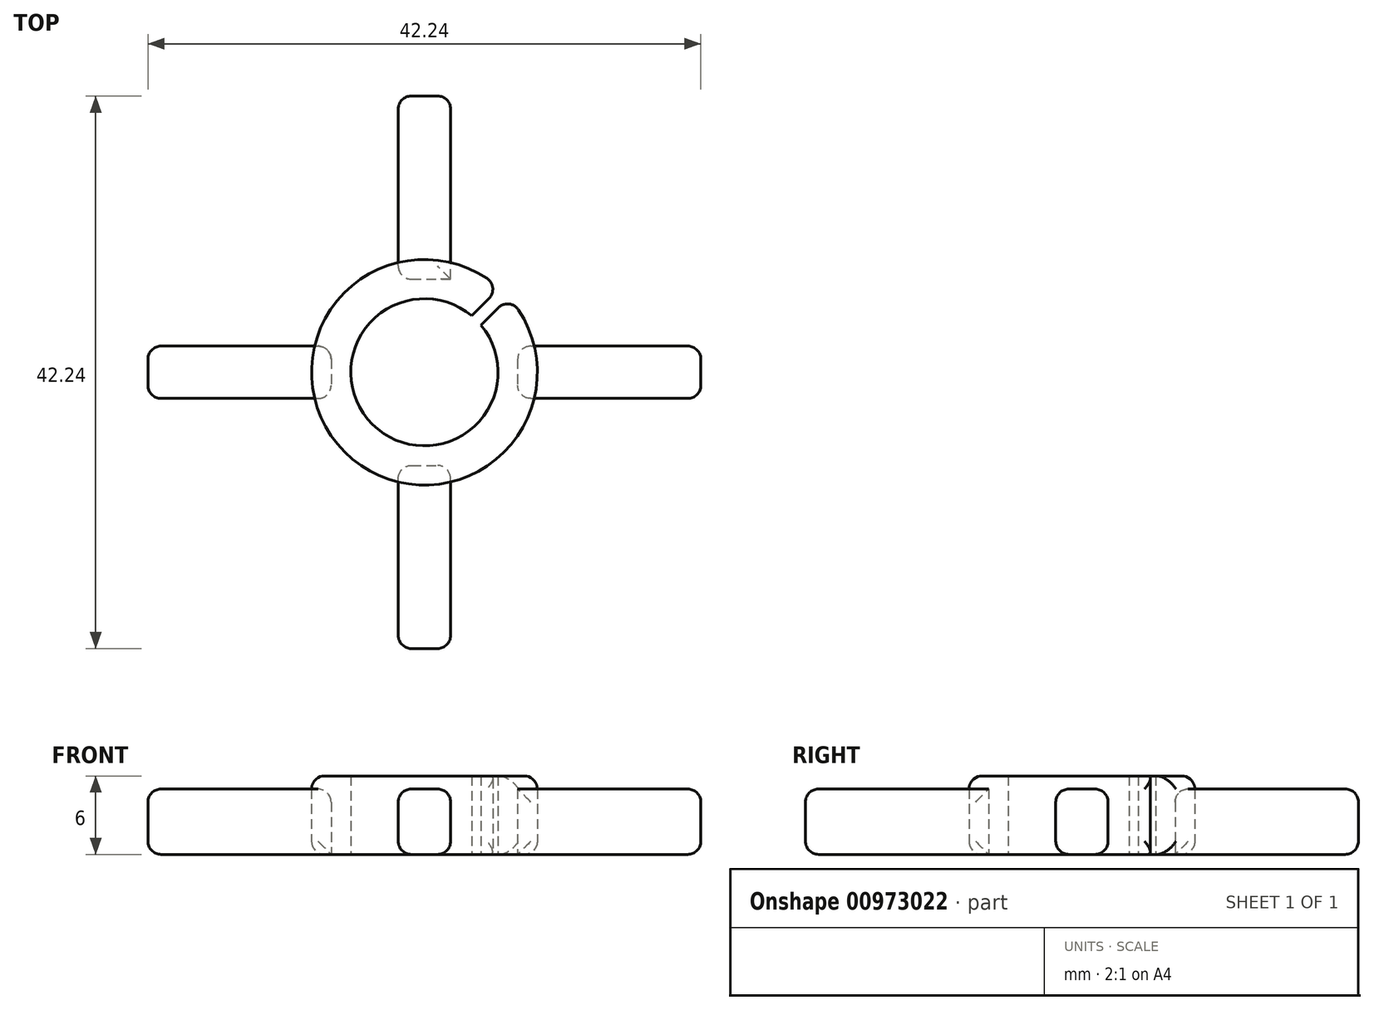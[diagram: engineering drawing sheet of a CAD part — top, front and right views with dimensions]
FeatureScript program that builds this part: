
annotation { "Feature Type Name" : "Feature", "Feature Type Description" : "" }
export const myFeature = defineFeature(function(context is Context, id is Id, definition is map)
    precondition{}
    {
        {
            var Q0;
            Q0=qCreatedBy(makeId("Top.planeOp"),FACE);
            var sketch = newSketch(context, id + "F0", { "sketchPlane" : qUnion([Q0])});
            skCircle(sketch, "E0", {"center": v(0, 0) * mm, "radius": 5.62 * mm});
            skCircle(sketch, "E1", {"center": v(0, 0) * mm, "radius": 8.62 * mm});
            skLineSegment(sketch, "E2.bottom", {"start": v(-21.12, 2) * mm, "end": v(-7.12, 2) * mm});
            skLineSegment(sketch, "E2.top", {"start": v(-21.12, -2) * mm, "end": v(-7.12, -2) * mm});
            skLineSegment(sketch, "E2.left", {"start": v(-21.12, 2) * mm, "end": v(-21.12, -2) * mm});
            skLineSegment(sketch, "E2.right", {"start": v(-7.12, 2) * mm, "end": v(-7.12, -2) * mm});
            skCircle(sketch, "E3", {"center": v(0, 0) * mm, "radius": 7.12 * mm, "construction": true});
            skPoint(sketch, "E4", {"position": v(-7.12, 0) * mm});
            skPoint(sketch, "E5", {"position": v(0, 7.12) * mm});
            skPoint(sketch, "E6", {"position": v(7.12, 0) * mm});
            skPoint(sketch, "E7", {"position": v(0, -7.12) * mm});
            skLineSegment(sketch, "E8.bottom", {"start": v(-2, 7.12) * mm, "end": v(-2, 21.12) * mm});
            skLineSegment(sketch, "E8.top", {"start": v(2, 7.12) * mm, "end": v(2, 21.12) * mm});
            skLineSegment(sketch, "E8.left", {"start": v(-2, 7.12) * mm, "end": v(2, 7.12) * mm});
            skLineSegment(sketch, "E8.right", {"start": v(-2, 21.12) * mm, "end": v(2, 21.12) * mm});
            skPoint(sketch, "E9", {"position": v(0, 21.12) * mm});
            skLineSegment(sketch, "E10.bottom", {"start": v(7.12, 2) * mm, "end": v(21.12, 2) * mm});
            skLineSegment(sketch, "E10.top", {"start": v(7.12, -2) * mm, "end": v(21.12, -2) * mm});
            skLineSegment(sketch, "E10.left", {"start": v(7.13, 2) * mm, "end": v(7.13, -2) * mm});
            skLineSegment(sketch, "E10.right", {"start": v(21.12, 2) * mm, "end": v(21.12, -2) * mm});
            skPoint(sketch, "E11", {"position": v(21.12, 0) * mm});
            skLineSegment(sketch, "E12.bottom", {"start": v(-2, -21.12) * mm, "end": v(-2, -7.12) * mm});
            skLineSegment(sketch, "E12.top", {"start": v(2, -21.12) * mm, "end": v(2, -7.12) * mm});
            skLineSegment(sketch, "E12.left", {"start": v(-2, -21.12) * mm, "end": v(2, -21.12) * mm});
            skLineSegment(sketch, "E12.right", {"start": v(-2, -7.12) * mm, "end": v(2, -7.12) * mm});
            skLineSegment(sketch, "E13.bottom", {"start": v(-0.35, 0.35) * mm, "end": v(0.35, -0.35) * mm});
            skLineSegment(sketch, "E13.top", {"start": v(13.79, 14.5) * mm, "end": v(14.5, 13.79) * mm});
            skLineSegment(sketch, "E13.left", {"start": v(-0.35, 0.35) * mm, "end": v(13.79, 14.5) * mm});
            skLineSegment(sketch, "E13.right", {"start": v(0.35, -0.35) * mm, "end": v(14.5, 13.79) * mm});
            skSolve(sketch);
        }
        {
            var Q0;
            {var subQ5=sQuery(id+"F0.wireOp",EDGE,"E2.right");Q0=makeQuery(id+"F0.imprint","IMPRINT",FACE,{"disambiguationData":[TD([[makeQuery(id+"F0.imprint","IMPRINT",EDGE,{"derivedFrom":subQ5}),-1.0]])]});}
            var Q1;
            {var subQ5=sQuery(id+"F0.wireOp",EDGE,"E8.left");Q1=makeQuery(id+"F0.imprint","IMPRINT",FACE,{"disambiguationData":[TD([[makeQuery(id+"F0.imprint","IMPRINT",EDGE,{"derivedFrom":subQ5}),1.0]])]});}
            var Q2;
            {var subQ5=sQuery(id+"F0.wireOp",EDGE,"E12.left");Q2=makeQuery(id+"F0.imprint","IMPRINT",FACE,{"disambiguationData":[TD([[makeQuery(id+"F0.imprint","IMPRINT",EDGE,{"derivedFrom":subQ5}),1.0]])]});}
            var Q3;
            {var subQ5=sQuery(id+"F0.wireOp",EDGE,"E12.right");Q3=makeQuery(id+"F0.imprint","IMPRINT",FACE,{"disambiguationData":[TD([[makeQuery(id+"F0.imprint","IMPRINT",EDGE,{"derivedFrom":subQ5}),-1.0]])]});}
            var Q4;
            {var subQ5=sQuery(id+"F0.wireOp",EDGE,"E10.right");Q4=makeQuery(id+"F0.imprint","IMPRINT",FACE,{"disambiguationData":[TD([[makeQuery(id+"F0.imprint","IMPRINT",EDGE,{"derivedFrom":subQ5}),-1.0]])]});}
            var Q5;
            {var subQ5=sQuery(id+"F0.wireOp",EDGE,"E10.left");Q5=makeQuery(id+"F0.imprint","IMPRINT",FACE,{"disambiguationData":[TD([[makeQuery(id+"F0.imprint","IMPRINT",EDGE,{"derivedFrom":subQ5}),1.0]])]});}
            var Q6;
            {var subQ5=sQuery(id+"F0.wireOp",EDGE,"E2.left");Q6=makeQuery(id+"F0.imprint","IMPRINT",FACE,{"disambiguationData":[TD([[makeQuery(id+"F0.imprint","IMPRINT",EDGE,{"derivedFrom":subQ5}),1.0]])]});}
            var Q7;
            {var subQ5=sQuery(id+"F0.wireOp",EDGE,"E8.right");Q7=makeQuery(id+"F0.imprint","IMPRINT",FACE,{"disambiguationData":[TD([[makeQuery(id+"F0.imprint","IMPRINT",EDGE,{"derivedFrom":subQ5}),-1.0]])]});}
            extrude(context, id + "F1", {"entities" : qUnion([Q0, Q1, Q2, Q3, Q4, Q5, Q6, Q7]), "depth" : 5 * mm, "offsetDistance" : 25 * mm});
        }
        {
            var Q0;
            {var subQ21=sQuery(id+"F0.wireOp",EDGE,"E2.right");Q0=makeQuery(id+"F0.imprint","IMPRINT",FACE,{"disambiguationData":[TD([[makeQuery(id+"F0.imprint","IMPRINT",EDGE,{"derivedFrom":subQ21}),1.0]])]});}
            var Q1;
            {var subQ5=sQuery(id+"F0.wireOp",EDGE,"E12.right");Q1=makeQuery(id+"F0.imprint","IMPRINT",FACE,{"disambiguationData":[TD([[makeQuery(id+"F0.imprint","IMPRINT",EDGE,{"derivedFrom":subQ5}),-1.0]])]});}
            var Q2;
            {var subQ5=sQuery(id+"F0.wireOp",EDGE,"E10.left");Q2=makeQuery(id+"F0.imprint","IMPRINT",FACE,{"disambiguationData":[TD([[makeQuery(id+"F0.imprint","IMPRINT",EDGE,{"derivedFrom":subQ5}),1.0]])]});}
            var Q3;
            {var subQ5=sQuery(id+"F0.wireOp",EDGE,"E8.left");Q3=makeQuery(id+"F0.imprint","IMPRINT",FACE,{"disambiguationData":[TD([[makeQuery(id+"F0.imprint","IMPRINT",EDGE,{"derivedFrom":subQ5}),1.0]])]});}
            var Q4;
            {var subQ5=sQuery(id+"F0.wireOp",EDGE,"E2.right");Q4=makeQuery(id+"F0.imprint","IMPRINT",FACE,{"disambiguationData":[TD([[makeQuery(id+"F0.imprint","IMPRINT",EDGE,{"derivedFrom":subQ5}),-1.0]])]});}
            extrude(context, id + "F2", {"entities" : qUnion([Q0, Q1, Q2, Q3, Q4]), "depth" : 6 * mm, "offsetDistance" : 25 * mm});
        }
        {
            var Q0;
            {var subQ5=sQuery(id+"F0.wireOp",EDGE,"E13.top");Q0=makeQuery(id+"F0.imprint","IMPRINT",FACE,{"disambiguationData":[TD([[makeQuery(id+"F0.imprint","IMPRINT",EDGE,{"derivedFrom":subQ5}),-1.0]])]});}
            var Q1;
            {var subQ0=sQuery(id+"F0.wireOp",EDGE,"E13.left");var subQ1=sQuery(id+"F0.wireOp",EDGE,"E0");var subQ2=makeQuery(id+"F0.imprint","INTERSECT",VERTEX,{"derivedFrom":[subQ1,subQ0]});Q1=makeQuery(id+"F0.imprint","IMPRINT",FACE,{"disambiguationData":[TD([[makeQuery(id+"F0.imprint","IMPRINT",EDGE,{"disambiguationData":[TD([[subQ2,1.0]])],"derivedFrom":subQ1}),-1.0]])]});}
            var Q2;
            {var subQ5=sQuery(id+"F0.wireOp",EDGE,"E13.bottom");Q2=makeQuery(id+"F0.imprint","IMPRINT",FACE,{"disambiguationData":[TD([[makeQuery(id+"F0.imprint","IMPRINT",EDGE,{"derivedFrom":subQ5}),1.0]])]});}
            var Q3;
            Q3=makeQuery(id+"F2.opExtrude","CAP_FACE",FACE,{"disambiguationData":[OSD([sQuery(id+"F0.wireOp",EDGE,"E0"),sQuery(id+"F0.wireOp",EDGE,"E1"),sQuery(id+"F0.wireOp",EDGE,"E13.left"),sQuery(id+"F0.wireOp",EDGE,"E13.right")])],"isStart":false});
            extrude(context, id + "F3", {"entities" : qUnion([Q0, Q1, Q2]), "operationType" : NewBodyOperationType.REMOVE, "endBound" : BoundingType.UP_TO_SURFACE, "depth" : -25 * mm, "endBoundEntityFace" : qUnion([Q3]), "offsetDistance" : 25 * mm});
        }
        {
            var Q0;
            Q0=makeQuery(id+"F2.opExtrude","SWEPT_FACE",FACE,{"disambiguationData":[OSD([sQuery(id+"F0.wireOp",EDGE,"E1")])]});
            var Q1;
            Q1=makeQuery(id+"F1.opExtrude","SWEPT_FACE",FACE,{"disambiguationData":[OSD([sQuery(id+"F0.wireOp",EDGE,"E12.top")])]});
            var Q2;
            Q2=makeQuery(id+"F1.opExtrude","SWEPT_FACE",FACE,{"disambiguationData":[OSD([sQuery(id+"F0.wireOp",EDGE,"E12.bottom")])]});
            var Q3;
            Q3=makeQuery(id+"F1.opExtrude","SWEPT_FACE",FACE,{"disambiguationData":[OSD([sQuery(id+"F0.wireOp",EDGE,"E12.left")])]});
            var Q4;
            Q4=makeQuery(id+"F1.opExtrude","SWEPT_FACE",FACE,{"disambiguationData":[OSD([sQuery(id+"F0.wireOp",EDGE,"E8.bottom")])]});
            var Q5;
            Q5=makeQuery(id+"F1.opExtrude","CAP_FACE",FACE,{"disambiguationData":[OSD([sQuery(id+"F0.wireOp",EDGE,"E8.bottom"),sQuery(id+"F0.wireOp",EDGE,"E8.top"),sQuery(id+"F0.wireOp",EDGE,"E8.left"),sQuery(id+"F0.wireOp",EDGE,"E8.right")])],"isStart":false});
            var Q6;
            Q6=makeQuery(id+"F1.opExtrude","SWEPT_FACE",FACE,{"disambiguationData":[OSD([sQuery(id+"F0.wireOp",EDGE,"E8.right")])]});
            var Q7;
            Q7=makeQuery(id+"F1.opExtrude","SWEPT_FACE",FACE,{"disambiguationData":[OSD([sQuery(id+"F0.wireOp",EDGE,"E2.left")])]});
            var Q8;
            Q8=makeQuery(id+"F1.opExtrude","CAP_FACE",FACE,{"disambiguationData":[OSD([sQuery(id+"F0.wireOp",EDGE,"E2.bottom"),sQuery(id+"F0.wireOp",EDGE,"E2.top"),sQuery(id+"F0.wireOp",EDGE,"E2.left"),sQuery(id+"F0.wireOp",EDGE,"E2.right")])],"isStart":false});
            var Q9;
            Q9=makeQuery(id+"F1.opExtrude","SWEPT_FACE",FACE,{"disambiguationData":[OSD([sQuery(id+"F0.wireOp",EDGE,"E2.top")])]});
            var Q10;
            Q10=makeQuery(id+"F1.opExtrude","SWEPT_FACE",FACE,{"disambiguationData":[OSD([sQuery(id+"F0.wireOp",EDGE,"E2.bottom")])]});
            var Q11;
            Q11=makeQuery(id+"F1.opExtrude","SWEPT_FACE",FACE,{"disambiguationData":[OSD([sQuery(id+"F0.wireOp",EDGE,"E10.top")])]});
            var Q12;
            Q12=makeQuery(id+"F1.opExtrude","SWEPT_FACE",FACE,{"disambiguationData":[OSD([sQuery(id+"F0.wireOp",EDGE,"E10.right")])]});
            var Q13;
            Q13=makeQuery(id+"F1.opExtrude","SWEPT_FACE",FACE,{"disambiguationData":[OSD([sQuery(id+"F0.wireOp",EDGE,"E10.bottom")])]});
            var Q14;
            Q14=makeQuery(id+"F1.opExtrude","CAP_EDGE",EDGE,{"disambiguationData":[OSD([sQuery(id+"F0.wireOp",EDGE,"E8.top")])],"isStart":true});
            fillet(context, id + "F4", {"entities" : qUnion([Q0, Q1, Q2, Q3, Q4, Q5, Q6, Q7, Q8, Q9, Q10, Q11, Q12, Q13, Q14]), "radius" : 1 * mm, "tangentPropagation" : true, "allowEdgeOverflow" : false});
        }
    });
